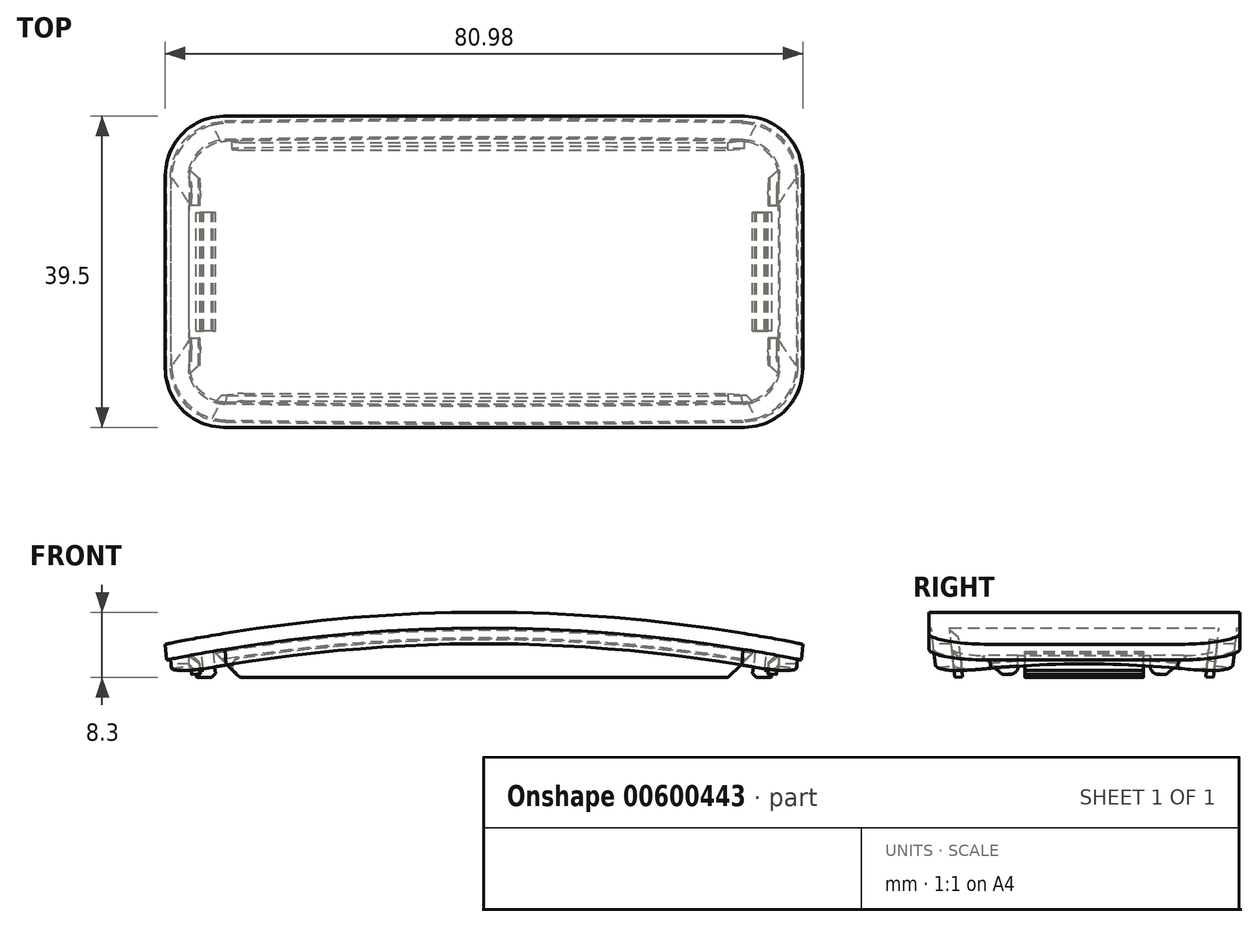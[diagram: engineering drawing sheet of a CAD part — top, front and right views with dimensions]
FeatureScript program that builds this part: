
annotation { "Feature Type Name" : "Feature", "Feature Type Description" : "" }
export const myFeature = defineFeature(function(context is Context, id is Id, definition is map)
    precondition{}
    {
        {
            var Q0;
            Q0=qCreatedBy(makeId("Top.planeOp"),FACE);
            var sketch = newSketch(context, id + "F0", { "sketchPlane" : qUnion([Q0])});
            skLineSegment(sketch, "E0.bottom", {"start": v(-32.64, 18.78) * mm, "end": v(32.64, 18.78) * mm});
            skLineSegment(sketch, "E0.top", {"start": v(-32.64, -18.78) * mm, "end": v(32.64, -18.78) * mm});
            skLineSegment(sketch, "E0.left", {"start": v(-39.64, 11.78) * mm, "end": v(-39.64, -11.78) * mm});
            skLineSegment(sketch, "E0.right", {"start": v(39.64, 11.78) * mm, "end": v(39.64, -11.78) * mm});
            skPoint(sketch, "E0.middle", {"position": v(0, 0) * mm});
            skPoint(sketch, "E1.visualSharp", {"position": v(-39.64, 18.78) * mm});
            skArc(sketch, "E1.filletArc", {"start": v(-32.64, 18.78) * mm, "mid": v(-37.59, 16.73) * mm, "end": v(-39.64, 11.78) * mm});
            skPoint(sketch, "E2.visualSharp", {"position": v(39.64, 18.78) * mm});
            skArc(sketch, "E2.filletArc", {"start": v(39.64, 11.78) * mm, "mid": v(37.59, 16.73) * mm, "end": v(32.64, 18.78) * mm});
            skPoint(sketch, "E3.visualSharp", {"position": v(39.64, -18.78) * mm});
            skArc(sketch, "E3.filletArc", {"start": v(32.64, -18.78) * mm, "mid": v(37.59, -16.73) * mm, "end": v(39.64, -11.78) * mm});
            skPoint(sketch, "E4.visualSharp", {"position": v(-39.64, -18.78) * mm});
            skArc(sketch, "E4.filletArc", {"start": v(-39.64, -11.78) * mm, "mid": v(-37.59, -16.73) * mm, "end": v(-32.64, -18.78) * mm});
            skSolve(sketch);
        }
        {
            var Q0;
            Q0=qCreatedBy(makeId("Top.planeOp"),FACE);
            cPlane(context, id + "F1", {"entities" : qUnion([Q0]), "cplaneType" : CPlaneType.OFFSET, "offset" : 100 * mm, "width" : 150 * mm, "height" : 150 * mm});
        }
        {
            var Q0;
            Q0=qCreatedBy(id+"F1.planeOp",FACE);
            var sketch = newSketch(context, id + "F2", { "sketchPlane" : qUnion([Q0])});
            skLineSegment(sketch, "E5.bottom", {"start": v(-40.98, 29.29) * mm, "end": v(40.98, 29.29) * mm});
            skLineSegment(sketch, "E5.top", {"start": v(-40.98, -29.29) * mm, "end": v(40.98, -29.29) * mm});
            skLineSegment(sketch, "E5.left", {"start": v(-48.38, 21.9) * mm, "end": v(-48.38, -21.9) * mm});
            skLineSegment(sketch, "E5.right", {"start": v(48.38, 21.9) * mm, "end": v(48.38, -21.9) * mm});
            skPoint(sketch, "E5.middle", {"position": v(0, 0) * mm});
            skPoint(sketch, "E6.visualSharp", {"position": v(-48.38, 29.29) * mm});
            skArc(sketch, "E6.filletArc", {"start": v(-40.98, 29.29) * mm, "mid": v(-46.22, 27.12) * mm, "end": v(-48.38, 21.9) * mm});
            skPoint(sketch, "E7.visualSharp", {"position": v(48.38, 29.29) * mm});
            skArc(sketch, "E7.filletArc", {"start": v(48.38, 21.9) * mm, "mid": v(46.22, 27.12) * mm, "end": v(40.98, 29.29) * mm});
            skPoint(sketch, "E8.visualSharp", {"position": v(48.38, -29.3) * mm});
            skArc(sketch, "E8.filletArc", {"start": v(40.98, -29.29) * mm, "mid": v(46.22, -27.12) * mm, "end": v(48.38, -21.9) * mm});
            skPoint(sketch, "E9.visualSharp", {"position": v(-48.38, -29.3) * mm});
            skArc(sketch, "E9.filletArc", {"start": v(-48.38, -21.9) * mm, "mid": v(-46.22, -27.12) * mm, "end": v(-40.98, -29.29) * mm});
            skSolve(sketch);
        }
        {
            var Q0;
            Q0=makeQuery(id+"F0.imprint","IMPRINT",FACE,{"disambiguationData":[TD([[makeQuery(id+"F0.imprint","IMPRINT",EDGE,{"derivedFrom":sQuery(id+"F0.wireOp",EDGE,"E0.bottom")}),-1.0]])]});
            var Q1;
            Q1=makeQuery(id+"F2.imprint","IMPRINT",FACE,{"disambiguationData":[TD([[makeQuery(id+"F2.imprint","IMPRINT",EDGE,{"derivedFrom":sQuery(id+"F2.wireOp",EDGE,"E5.bottom")}),-1.0]])]});
            loft(context, id + "F3", {"sheetProfilesArray" : [{ "sheetProfileEntities" : qUnion([Q0]) }, { "sheetProfileEntities" : qUnion([Q1]) }]});
        }
        {
            var Q0;
            Q0=makeQuery(id+"F3.opLoft","CAP_FACE",FACE,{"disambiguationData":[OSD([makeQuery(id+"F0.imprint","IMPRINT",FACE,{"disambiguationData":[TD([[makeQuery(id+"F0.imprint","IMPRINT",EDGE,{"derivedFrom":sQuery(id+"F0.wireOp",EDGE,"E0.bottom")}),-1.0]])]})])],"isStart":true});
            var Q1;
            Q1=makeQuery(id+"F3.opLoft","CAP_FACE",FACE,{"disambiguationData":[OSD([makeQuery(id+"F2.imprint","IMPRINT",FACE,{"disambiguationData":[TD([[makeQuery(id+"F2.imprint","IMPRINT",EDGE,{"derivedFrom":sQuery(id+"F2.wireOp",EDGE,"E5.bottom")}),-1.0]])]})])],"isStart":true});
            shell(context, id + "F4", {"entities" : qUnion([Q0, Q1]), "thickness" : 2.3 * mm});
        }
        {
            var Q0;
            Q0=qCreatedBy(makeId("Front.planeOp"),FACE);
            var sketch = newSketch(context, id + "F5", { "sketchPlane" : qUnion([Q0])});
            skArc(sketch, "E10", {"start": v(39.64, 0) * mm, "mid": v(0, 3.97) * mm, "end": v(-39.64, 0) * mm});
            skLineSegment(sketch, "E11", {"start": v(-39.64, 0) * mm, "end": v(39.64, 0) * mm});
            skSolve(sketch);
        }
        {
            var Q0;
            Q0=qSketchRegion(id+"F5",true);
            var Q1;
            Q1=makeQuery(id+"F3.opLoft","SWEPT_FACE",FACE,{"disambiguationData":[OSD([sQuery(id+"F0.wireOp",EDGE,"E0.bottom"),sQuery(id+"F0.wireOp",EDGE,"E1.filletArc"),sQuery(id+"F0.wireOp",EDGE,"E2.filletArc"),sQuery(id+"F2.wireOp",EDGE,"E5.bottom"),sQuery(id+"F2.wireOp",EDGE,"E6.filletArc"),sQuery(id+"F2.wireOp",EDGE,"E7.filletArc")])]});
            var Q2;
            Q2=makeQuery(id+"F3.opLoft","SWEPT_FACE",FACE,{"disambiguationData":[OSD([sQuery(id+"F0.wireOp",EDGE,"E0.top"),sQuery(id+"F0.wireOp",EDGE,"E3.filletArc"),sQuery(id+"F0.wireOp",EDGE,"E4.filletArc"),sQuery(id+"F2.wireOp",EDGE,"E5.top"),sQuery(id+"F2.wireOp",EDGE,"E8.filletArc"),sQuery(id+"F2.wireOp",EDGE,"E9.filletArc")])]});
            extrude(context, id + "F6", {"entities" : qUnion([Q0]), "operationType" : NewBodyOperationType.REMOVE, "endBound" : BoundingType.UP_TO_SURFACE, "oppositeDirection" : true, "depth" : 25 * mm, "endBoundEntityFace" : qUnion([Q1]), "offsetDistance" : 25 * mm, "hasSecondDirection" : true, "secondDirectionBound" : SecondDirectionBoundingType.UP_TO_SURFACE, "secondDirectionOppositeDirection" : false, "secondDirectionDepth" : 25 * mm, "secondDirectionBoundEntityFace" : qUnion([Q2])});
        }
        {
            var Q0;
            Q0=qCreatedBy(makeId("Right.planeOp"),FACE);
            var sketch = newSketch(context, id + "F7", { "sketchPlane" : qUnion([Q0])});
            skArc(sketch, "E12", {"start": v(18.78, 0) * mm, "mid": v(0, 1.42) * mm, "end": v(-18.78, 0) * mm});
            skLineSegment(sketch, "E13", {"start": v(-18.78, 0) * mm, "end": v(18.78, 0) * mm});
            skSolve(sketch);
        }
        {
            var Q0;
            Q0=qSketchRegion(id+"F7",true);
            var Q1;
            Q1=makeQuery(id+"F3.opLoft","SWEPT_FACE",FACE,{"disambiguationData":[OSD([sQuery(id+"F0.wireOp",EDGE,"E0.right"),sQuery(id+"F0.wireOp",EDGE,"E2.filletArc"),sQuery(id+"F0.wireOp",EDGE,"E3.filletArc"),sQuery(id+"F2.wireOp",EDGE,"E5.right"),sQuery(id+"F2.wireOp",EDGE,"E7.filletArc"),sQuery(id+"F2.wireOp",EDGE,"E8.filletArc")])]});
            var Q2;
            Q2=makeQuery(id+"F3.opLoft","SWEPT_FACE",FACE,{"disambiguationData":[OSD([sQuery(id+"F0.wireOp",EDGE,"E0.left"),sQuery(id+"F0.wireOp",EDGE,"E1.filletArc"),sQuery(id+"F0.wireOp",EDGE,"E4.filletArc"),sQuery(id+"F2.wireOp",EDGE,"E5.left"),sQuery(id+"F2.wireOp",EDGE,"E6.filletArc"),sQuery(id+"F2.wireOp",EDGE,"E9.filletArc")])]});
            extrude(context, id + "F8", {"entities" : qUnion([Q0]), "operationType" : NewBodyOperationType.REMOVE, "endBound" : BoundingType.UP_TO_SURFACE, "depth" : 25 * mm, "endBoundEntityFace" : qUnion([Q1]), "offsetDistance" : 25 * mm, "hasSecondDirection" : true, "secondDirectionBound" : SecondDirectionBoundingType.UP_TO_SURFACE, "secondDirectionOppositeDirection" : true, "secondDirectionDepth" : 25 * mm, "secondDirectionBoundEntityFace" : qUnion([Q2])});
        }
        {
            var Q0;
            Q0=makeQuery(id+"F8.boolean.opBoolean","INTERSECT",EDGE,{"disambiguationData":[OD(2.0)],"derivedFrom":[makeQuery(id+"F6.boolean.opBoolean","COPY",FACE,{"derivedFrom":makeQuery(id+"F6.opExtrude","SWEPT_FACE",FACE,{"disambiguationData":[OSD([sQuery(id+"F5.wireOp",EDGE,"E10")])]})}),makeQuery(id+"F8.opExtrude","SWEPT_FACE",FACE,{"disambiguationData":[OSD([sQuery(id+"F7.wireOp",EDGE,"E12")])]})]});
            var Q1;
            Q1=makeQuery(id+"F8.boolean.opBoolean","INTERSECT",EDGE,{"disambiguationData":[OD(3.0)],"derivedFrom":[makeQuery(id+"F6.boolean.opBoolean","COPY",FACE,{"derivedFrom":makeQuery(id+"F6.opExtrude","SWEPT_FACE",FACE,{"disambiguationData":[OSD([sQuery(id+"F5.wireOp",EDGE,"E10")])]})}),makeQuery(id+"F8.opExtrude","SWEPT_FACE",FACE,{"disambiguationData":[OSD([sQuery(id+"F7.wireOp",EDGE,"E12")])]})]});
            var Q2;
            Q2=makeQuery(id+"F8.boolean.opBoolean","INTERSECT",EDGE,{"disambiguationData":[OD(0.0)],"derivedFrom":[makeQuery(id+"F6.boolean.opBoolean","COPY",FACE,{"derivedFrom":makeQuery(id+"F6.opExtrude","SWEPT_FACE",FACE,{"disambiguationData":[OSD([sQuery(id+"F5.wireOp",EDGE,"E10")])]})}),makeQuery(id+"F8.opExtrude","SWEPT_FACE",FACE,{"disambiguationData":[OSD([sQuery(id+"F7.wireOp",EDGE,"E12")])]})]});
            var Q3;
            Q3=makeQuery(id+"F8.boolean.opBoolean","INTERSECT",EDGE,{"disambiguationData":[OD(1.0)],"derivedFrom":[makeQuery(id+"F6.boolean.opBoolean","COPY",FACE,{"derivedFrom":makeQuery(id+"F6.opExtrude","SWEPT_FACE",FACE,{"disambiguationData":[OSD([sQuery(id+"F5.wireOp",EDGE,"E10")])]})}),makeQuery(id+"F8.opExtrude","SWEPT_FACE",FACE,{"disambiguationData":[OSD([sQuery(id+"F7.wireOp",EDGE,"E12")])]})]});
            fillet(context, id + "F9", {"entities" : qUnion([Q0, Q1, Q2, Q3]), "radius" : 40 * mm, "tangentPropagation" : true, "allowEdgeOverflow" : false});
        }
        {
            var Q0;
            Q0=qCreatedBy(makeId("Front.planeOp"),FACE);
            var sketch = newSketch(context, id + "F10", { "sketchPlane" : qUnion([Q0])});
            skLineSegment(sketch, "E14.bottom", {"start": v(-48.38, 100) * mm, "end": v(48.38, 100) * mm});
            skLineSegment(sketch, "E14.top", {"start": v(-48.38, 20.57) * mm, "end": v(48.38, 20.57) * mm});
            skLineSegment(sketch, "E14.left", {"start": v(-48.38, 100) * mm, "end": v(-48.38, 20.57) * mm});
            skLineSegment(sketch, "E14.right", {"start": v(48.38, 100) * mm, "end": v(48.38, 20.57) * mm});
            skSolve(sketch);
        }
        {
            var Q0;
            Q0=qSketchRegion(id+"F10",true);
            var Q1;
            Q1=makeQuery(id+"F3.opLoft","SWEPT_FACE",FACE,{"disambiguationData":[OSD([sQuery(id+"F0.wireOp",EDGE,"E0.bottom"),sQuery(id+"F0.wireOp",EDGE,"E1.filletArc"),sQuery(id+"F0.wireOp",EDGE,"E2.filletArc"),sQuery(id+"F2.wireOp",EDGE,"E5.bottom"),sQuery(id+"F2.wireOp",EDGE,"E6.filletArc"),sQuery(id+"F2.wireOp",EDGE,"E7.filletArc")])]});
            var Q2;
            Q2=makeQuery(id+"F3.opLoft","SWEPT_FACE",FACE,{"disambiguationData":[OSD([sQuery(id+"F0.wireOp",EDGE,"E0.top"),sQuery(id+"F0.wireOp",EDGE,"E3.filletArc"),sQuery(id+"F0.wireOp",EDGE,"E4.filletArc"),sQuery(id+"F2.wireOp",EDGE,"E5.top"),sQuery(id+"F2.wireOp",EDGE,"E8.filletArc"),sQuery(id+"F2.wireOp",EDGE,"E9.filletArc")])]});
            extrude(context, id + "F11", {"entities" : qUnion([Q0]), "operationType" : NewBodyOperationType.REMOVE, "endBound" : BoundingType.UP_TO_SURFACE, "oppositeDirection" : true, "depth" : 25 * mm, "endBoundEntityFace" : qUnion([Q1]), "offsetDistance" : 25 * mm, "hasSecondDirection" : true, "secondDirectionBound" : SecondDirectionBoundingType.UP_TO_SURFACE, "secondDirectionOppositeDirection" : false, "secondDirectionDepth" : 25 * mm, "secondDirectionBoundEntityFace" : qUnion([Q2])});
        }
        {
            var Q0;
            Q0=makeQuery(id+"F4.opShell","OFFSET_FACE",FACE,{"disambiguationData":[OSD([sQuery(id+"F0.wireOp",EDGE,"E0.bottom"),sQuery(id+"F0.wireOp",EDGE,"E1.filletArc"),sQuery(id+"F0.wireOp",EDGE,"E2.filletArc"),sQuery(id+"F2.wireOp",EDGE,"E5.bottom"),sQuery(id+"F2.wireOp",EDGE,"E6.filletArc"),sQuery(id+"F2.wireOp",EDGE,"E7.filletArc")])]});
            var sketch = newSketch(context, id + "F12", { "sketchPlane" : qUnion([Q0])});
            skArc(sketch, "E15", {"start": v(33.1, 3.47) * mm, "mid": v(0, 6.2) * mm, "end": v(-33.1, 3.47) * mm});
            skLineSegment(sketch, "E16", {"start": v(31.01, 1.4) * mm, "end": v(33.1, 3.47) * mm});
            skLineSegment(sketch, "E17", {"start": v(0, 6.2) * mm, "end": v(0, 5.7) * mm, "construction": true});
            skLineSegment(sketch, "E18", {"start": v(0, 5.7) * mm, "end": v(0, 1.4) * mm, "construction": true});
            skLineSegment(sketch, "E19", {"start": v(-33.1, 3.47) * mm, "end": v(-31.01, 1.4) * mm});
            skLineSegment(sketch, "E20", {"start": v(33.1, 3.47) * mm, "end": v(31.01, 1.4) * mm});
            skLineSegment(sketch, "E21", {"start": v(-31.01, 1.4) * mm, "end": v(31.01, 1.4) * mm});
            skSolve(sketch);
        }
        {
            var Q0;
            Q0=qSketchRegion(id+"F12",true);
            extrude(context, id + "F13", {"entities" : qUnion([Q0]), "depth" : 1 * mm, "offsetDistance" : 25 * mm});
        }
        {
            var Q0;
            Q0=makeQuery(id+"F13.opExtrude","SWEPT_BODY",BODY,{"disambiguationData":[OSD([sQuery(id+"F12.wireOp",EDGE,"E15"),sQuery(id+"F12.wireOp",EDGE,"fm1ZzIcU-osaq-4KBk-rcFe-HOcxulJE4Vdi"),sQuery(id+"F12.wireOp",EDGE,"E19"),sQuery(id+"F12.wireOp",EDGE,"E20")])]});
            var Q1;
            Q1=qCreatedBy(makeId("Front.planeOp"),FACE);
            mirror(context, id + "F14", {"operationType" : NewBodyOperationType.ADD, "entities" : qUnion([Q0]), "mirrorPlane" : qUnion([Q1])});
        }
        {
            var Q0;
            Q0=makeQuery(id+"F4.opShell","OFFSET_FACE",FACE,{"disambiguationData":[OSD([sQuery(id+"F0.wireOp",EDGE,"E0.left"),sQuery(id+"F0.wireOp",EDGE,"E1.filletArc"),sQuery(id+"F0.wireOp",EDGE,"E4.filletArc"),sQuery(id+"F2.wireOp",EDGE,"E5.left"),sQuery(id+"F2.wireOp",EDGE,"E6.filletArc"),sQuery(id+"F2.wireOp",EDGE,"E9.filletArc")])]});
            var sketch = newSketch(context, id + "F15", { "sketchPlane" : qUnion([Q0])});
            skArc(sketch, "E22", {"start": v(11.9, 4.62) * mm, "mid": v(0, 5.18) * mm, "end": v(-11.9, 4.62) * mm});
            skLineSegment(sketch, "E23", {"start": v(0, 4.68) * mm, "end": v(0, 5.18) * mm, "construction": true});
            skLineSegment(sketch, "E24", {"start": v(-11.9, 4.62) * mm, "end": v(-10.4, 3.25) * mm});
            skLineSegment(sketch, "E25", {"start": v(11.9, 4.62) * mm, "end": v(10.4, 3.25) * mm});
            skArc(sketch, "E26", {"start": v(10.4, 3.25) * mm, "mid": v(0, 3.68) * mm, "end": v(-10.4, 3.25) * mm});
            skLineSegment(sketch, "E27", {"start": v(8.4, 3.4) * mm, "end": v(8.4, 4.9) * mm});
            skLineSegment(sketch, "E28", {"start": v(-8.4, 3.4) * mm, "end": v(-8.4, 4.9) * mm});
            skSolve(sketch);
        }
        {
            var Q0;
            {var subQ7=sQuery(id+"F15.wireOp",EDGE,"E26");var subQ9=sQuery(id+"F15.wireOp",EDGE,"E25");var subQ10=makeQuery(id+"F15.imprint","INTERSECT",VERTEX,{"derivedFrom":[subQ9,subQ7]});Q0=makeQuery(id+"F15.imprint","IMPRINT",FACE,{"disambiguationData":[TD([[makeQuery(id+"F15.imprint","IMPRINT",EDGE,{"disambiguationData":[TD([[subQ10,-1.0]])],"derivedFrom":subQ7}),-1.0]])]});}
            var Q1;
            {var subQ0=sQuery(id+"F15.wireOp",EDGE,"E27");var subQ1=sQuery(id+"F15.wireOp",EDGE,"E22");var subQ2=makeQuery(id+"F15.imprint","INTERSECT",VERTEX,{"derivedFrom":[subQ1,subQ0]});Q1=makeQuery(id+"F15.imprint","IMPRINT",FACE,{"disambiguationData":[TD([[makeQuery(id+"F15.imprint","IMPRINT",EDGE,{"disambiguationData":[TD([[subQ2,1.0]])],"derivedFrom":subQ1}),1.0]])]});}
            var Q2;
            {var subQ7=sQuery(id+"F15.wireOp",EDGE,"E26");var subQ9=sQuery(id+"F15.wireOp",EDGE,"E24");var subQ10=makeQuery(id+"F15.imprint","INTERSECT",VERTEX,{"derivedFrom":[subQ9,subQ7]});Q2=makeQuery(id+"F15.imprint","IMPRINT",FACE,{"disambiguationData":[TD([[makeQuery(id+"F15.imprint","IMPRINT",EDGE,{"disambiguationData":[TD([[subQ10,1.0]])],"derivedFrom":subQ7}),-1.0]])]});}
            var Q3;
            {var subQ9=sQuery(id+"F15.wireOp",EDGE,"E28");var subQ11=sQuery(id+"F15.wireOp",EDGE,"E22");var subQ12=makeQuery(id+"F15.imprint","INTERSECT",VERTEX,{"derivedFrom":[subQ11,subQ9]});Q3=makeQuery(id+"F15.imprint","IMPRINT",FACE,{"disambiguationData":[TD([[makeQuery(id+"F15.imprint","IMPRINT",EDGE,{"disambiguationData":[TD([[subQ12,-1.0]])],"derivedFrom":subQ11}),1.0]])]});}
            extrude(context, id + "F16", {"entities" : qUnion([Q0, Q1, Q2, Q3]), "depth" : 1.3 * mm, "offsetDistance" : 25 * mm});
        }
        {
            var Q0;
            Q0=makeQuery(id+"F16.opExtrude","SWEPT_BODY",BODY,{"disambiguationData":[OSD([sQuery(id+"F15.wireOp",EDGE,"E22"),sQuery(id+"F15.wireOp",EDGE,"E24"),sQuery(id+"F15.wireOp",EDGE,"E25"),sQuery(id+"F15.wireOp",EDGE,"E26")])]});
            var Q1;
            Q1=qCreatedBy(makeId("Right.planeOp"),FACE);
            mirror(context, id + "F17", {"operationType" : NewBodyOperationType.ADD, "entities" : qUnion([Q0]), "mirrorPlane" : qUnion([Q1])});
        }
        {
            var Q0;
            Q0=makeQuery(id+"F16.opExtrude","CAP_FACE",FACE,{"disambiguationData":[OSD([sQuery(id+"F15.wireOp",EDGE,"E22"),sQuery(id+"F15.wireOp",EDGE,"E25"),sQuery(id+"F15.wireOp",EDGE,"E26"),sQuery(id+"F15.wireOp",EDGE,"E27")])],"isStart":true});
            var Q1;
            Q1=makeQuery(id+"F16.opExtrude","CAP_FACE",FACE,{"disambiguationData":[OSD([sQuery(id+"F15.wireOp",EDGE,"E22"),sQuery(id+"F15.wireOp",EDGE,"E24"),sQuery(id+"F15.wireOp",EDGE,"E26"),sQuery(id+"F15.wireOp",EDGE,"E28")])],"isStart":true});
            extrude(context, id + "F18", {"entities" : qUnion([Q0, Q1]), "operationType" : NewBodyOperationType.REMOVE, "oppositeDirection" : true, "depth" : .2 * mm, "offsetDistance" : 25 * mm});
        }
        {
            var Q0;
            Q0=makeQuery(id+"F17.opPattern","COPY",FACE,{"derivedFrom":makeQuery(id+"F16.opExtrude","CAP_FACE",FACE,{"disambiguationData":[OSD([sQuery(id+"F15.wireOp",EDGE,"E22"),sQuery(id+"F15.wireOp",EDGE,"E25"),sQuery(id+"F15.wireOp",EDGE,"E26"),sQuery(id+"F15.wireOp",EDGE,"E27")])],"isStart":true}),"instanceName":"1"});
            var Q1;
            Q1=makeQuery(id+"F17.opPattern","COPY",FACE,{"derivedFrom":makeQuery(id+"F16.opExtrude","CAP_FACE",FACE,{"disambiguationData":[OSD([sQuery(id+"F15.wireOp",EDGE,"E22"),sQuery(id+"F15.wireOp",EDGE,"E24"),sQuery(id+"F15.wireOp",EDGE,"E26"),sQuery(id+"F15.wireOp",EDGE,"E28")])],"isStart":true}),"instanceName":"1"});
            extrude(context, id + "F19", {"entities" : qUnion([Q0, Q1]), "operationType" : NewBodyOperationType.REMOVE, "oppositeDirection" : true, "depth" : .2 * mm, "offsetDistance" : 25 * mm});
        }
        {
            var Q0;
            Q0=makeQuery(id+"F16.opExtrude","CAP_EDGE",EDGE,{"disambiguationData":[OSD([sQuery(id+"F15.wireOp",EDGE,"E22")])],"isStart":true});
            var Q1;
            Q1=makeQuery(id+"F13.opExtrude","CAP_EDGE",EDGE,{"disambiguationData":[OSD([sQuery(id+"F12.wireOp",EDGE,"E15")])],"isStart":true});
            var Q2;
            Q2=makeQuery(id+"F17.opPattern","COPY",EDGE,{"derivedFrom":makeQuery(id+"F16.opExtrude","CAP_EDGE",EDGE,{"disambiguationData":[OSD([sQuery(id+"F15.wireOp",EDGE,"E22")])],"isStart":true}),"instanceName":"1"});
            var Q3;
            Q3=makeQuery(id+"F14.opPattern","COPY",EDGE,{"derivedFrom":makeQuery(id+"F13.opExtrude","CAP_EDGE",EDGE,{"disambiguationData":[OSD([sQuery(id+"F12.wireOp",EDGE,"E15")])],"isStart":true}),"instanceName":"1"});
            chamfer(context, id + "F20", {"entities" : qUnion([Q0, Q1, Q2, Q3]), "width" : 1.2 * mm, "tangentPropagation" : true});
        }
        {
            var Q0;
            Q0=makeQuery(id+"F13.opExtrude","SWEPT_EDGE",EDGE,{"disambiguationData":[OSD([sQuery(id+"F12.wireOp",EDGE,"fm1ZzIcU-osaq-4KBk-rcFe-HOcxulJE4Vdi"),sQuery(id+"F12.wireOp",EDGE,"E19")])]});
            var Q1;
            Q1=makeQuery(id+"F16.opExtrude","SWEPT_EDGE",EDGE,{"disambiguationData":[OSD([sQuery(id+"F15.wireOp",EDGE,"E25"),sQuery(id+"F15.wireOp",EDGE,"E26")])]});
            var Q2;
            Q2=makeQuery(id+"F13.opExtrude","SWEPT_EDGE",EDGE,{"disambiguationData":[OSD([sQuery(id+"F12.wireOp",EDGE,"fm1ZzIcU-osaq-4KBk-rcFe-HOcxulJE4Vdi"),sQuery(id+"F12.wireOp",EDGE,"E20")])]});
            var Q3;
            Q3=makeQuery(id+"F17.opPattern","COPY",EDGE,{"derivedFrom":makeQuery(id+"F16.opExtrude","SWEPT_EDGE",EDGE,{"disambiguationData":[OSD([sQuery(id+"F15.wireOp",EDGE,"E25"),sQuery(id+"F15.wireOp",EDGE,"E26")])]}),"instanceName":"1"});
            var Q4;
            Q4=makeQuery(id+"F17.opPattern","COPY",EDGE,{"derivedFrom":makeQuery(id+"F16.opExtrude","SWEPT_EDGE",EDGE,{"disambiguationData":[OSD([sQuery(id+"F15.wireOp",EDGE,"E24"),sQuery(id+"F15.wireOp",EDGE,"E26")])]}),"instanceName":"1"});
            var Q5;
            Q5=makeQuery(id+"F14.opPattern","COPY",EDGE,{"derivedFrom":makeQuery(id+"F13.opExtrude","SWEPT_EDGE",EDGE,{"disambiguationData":[OSD([sQuery(id+"F12.wireOp",EDGE,"fm1ZzIcU-osaq-4KBk-rcFe-HOcxulJE4Vdi"),sQuery(id+"F12.wireOp",EDGE,"E20")])]}),"instanceName":"1"});
            var Q6;
            Q6=makeQuery(id+"F14.opPattern","COPY",EDGE,{"derivedFrom":makeQuery(id+"F13.opExtrude","SWEPT_EDGE",EDGE,{"disambiguationData":[OSD([sQuery(id+"F12.wireOp",EDGE,"fm1ZzIcU-osaq-4KBk-rcFe-HOcxulJE4Vdi"),sQuery(id+"F12.wireOp",EDGE,"E19")])]}),"instanceName":"1"});
            var Q7;
            Q7=makeQuery(id+"F16.opExtrude","SWEPT_EDGE",EDGE,{"disambiguationData":[OSD([sQuery(id+"F15.wireOp",EDGE,"E24"),sQuery(id+"F15.wireOp",EDGE,"E26")])]});
            var Q8;
            Q8=makeQuery(id+"F16.opExtrude","SWEPT_EDGE",EDGE,{"disambiguationData":[OSD([sQuery(id+"F15.wireOp",EDGE,"E26"),sQuery(id+"F15.wireOp",EDGE,"E27")])]});
            var Q9;
            Q9=makeQuery(id+"F16.opExtrude","SWEPT_EDGE",EDGE,{"disambiguationData":[OSD([sQuery(id+"F15.wireOp",EDGE,"E26"),sQuery(id+"F15.wireOp",EDGE,"E28")])]});
            var Q10;
            Q10=makeQuery(id+"F17.opPattern","COPY",EDGE,{"derivedFrom":makeQuery(id+"F16.opExtrude","SWEPT_EDGE",EDGE,{"disambiguationData":[OSD([sQuery(id+"F15.wireOp",EDGE,"E26"),sQuery(id+"F15.wireOp",EDGE,"E28")])]}),"instanceName":"1"});
            var Q11;
            Q11=makeQuery(id+"F17.opPattern","COPY",EDGE,{"derivedFrom":makeQuery(id+"F16.opExtrude","SWEPT_EDGE",EDGE,{"disambiguationData":[OSD([sQuery(id+"F15.wireOp",EDGE,"E26"),sQuery(id+"F15.wireOp",EDGE,"E27")])]}),"instanceName":"1"});
            fillet(context, id + "F21", {"entities" : qUnion([Q0, Q1, Q2, Q3, Q4, Q5, Q6, Q7, Q8, Q9, Q10, Q11]), "radius" : 1 * mm, "tangentPropagation" : true, "allowEdgeOverflow" : false});
        }
        {
            var Q0;
            Q0=qCreatedBy(makeId("Front.planeOp"),FACE);
            var sketch = newSketch(context, id + "F22", { "sketchPlane" : qUnion([Q0])});
            skArc(sketch, "E29", {"start": v(41.94, 1.57) * mm, "mid": v(0, 5.97) * mm, "end": v(-41.94, 1.57) * mm});
            skLineSegment(sketch, "E30", {"start": v(-41.94, 1.57) * mm, "end": v(-41.94, 20.57) * mm});
            skLineSegment(sketch, "E31", {"start": v(-41.94, 20.57) * mm, "end": v(41.94, 20.57) * mm});
            skLineSegment(sketch, "E32", {"start": v(41.94, 20.57) * mm, "end": v(41.94, 1.57) * mm});
            skSolve(sketch);
        }
        {
            var Q0;
            Q0=qSketchRegion(id+"F22",true);
            var Q1;
            Q1=makeQuery(id+"F3.opLoft","SWEPT_FACE",FACE,{"disambiguationData":[OSD([sQuery(id+"F0.wireOp",EDGE,"E0.bottom"),sQuery(id+"F0.wireOp",EDGE,"E1.filletArc"),sQuery(id+"F0.wireOp",EDGE,"E2.filletArc"),sQuery(id+"F2.wireOp",EDGE,"E5.bottom"),sQuery(id+"F2.wireOp",EDGE,"E6.filletArc"),sQuery(id+"F2.wireOp",EDGE,"E7.filletArc")])]});
            var Q2;
            Q2=makeQuery(id+"F3.opLoft","SWEPT_FACE",FACE,{"disambiguationData":[OSD([sQuery(id+"F0.wireOp",EDGE,"E0.top"),sQuery(id+"F0.wireOp",EDGE,"E3.filletArc"),sQuery(id+"F0.wireOp",EDGE,"E4.filletArc"),sQuery(id+"F2.wireOp",EDGE,"E5.top"),sQuery(id+"F2.wireOp",EDGE,"E8.filletArc"),sQuery(id+"F2.wireOp",EDGE,"E9.filletArc")])]});
            extrude(context, id + "F23", {"entities" : qUnion([Q0]), "operationType" : NewBodyOperationType.REMOVE, "endBound" : BoundingType.UP_TO_SURFACE, "oppositeDirection" : true, "depth" : 25 * mm, "endBoundEntityFace" : qUnion([Q1]), "offsetDistance" : 25 * mm, "hasSecondDirection" : true, "secondDirectionBound" : SecondDirectionBoundingType.UP_TO_SURFACE, "secondDirectionOppositeDirection" : false, "secondDirectionDepth" : 25 * mm, "secondDirectionBoundEntityFace" : qUnion([Q2])});
        }
        {
            var Q0;
            Q0=qCreatedBy(makeId("Front.planeOp"),FACE);
            var sketch = newSketch(context, id + "F24", { "sketchPlane" : qUnion([Q0])});
            skArc(sketch, "E33", {"start": v(40.49, 3.9) * mm, "mid": v(0, 7.97) * mm, "end": v(-40.49, 3.9) * mm});
            skLineSegment(sketch, "E34", {"start": v(-40.31, 1.9) * mm, "end": v(-40.49, 3.9) * mm});
            skLineSegment(sketch, "E35", {"start": v(40.31, 1.9) * mm, "end": v(40.49, 3.9) * mm});
            skArc(sketch, "E36", {"start": v(40.31, 1.9) * mm, "mid": v(0, 5.97) * mm, "end": v(-40.31, 1.9) * mm});
            skLineSegment(sketch, "E37", {"start": v(0, 5.97) * mm, "end": v(0, 7.97) * mm, "construction": true});
            skLineSegment(sketch, "E38", {"start": v(39.71, 0.85) * mm, "end": v(39.81, 2) * mm, "construction": true});
            skSolve(sketch);
        }
        {
            var Q0;
            Q0=qSketchRegion(id+"F24",true);
            var Q1;
            Q1=makeQuery(id+"F3.opLoft","SWEPT_FACE",FACE,{"disambiguationData":[OSD([sQuery(id+"F0.wireOp",EDGE,"E0.top"),sQuery(id+"F0.wireOp",EDGE,"E3.filletArc"),sQuery(id+"F0.wireOp",EDGE,"E4.filletArc"),sQuery(id+"F2.wireOp",EDGE,"E5.top"),sQuery(id+"F2.wireOp",EDGE,"E8.filletArc"),sQuery(id+"F2.wireOp",EDGE,"E9.filletArc")])]});
            var Q2;
            Q2=makeQuery(id+"F3.opLoft","SWEPT_FACE",FACE,{"disambiguationData":[OSD([sQuery(id+"F0.wireOp",EDGE,"E0.bottom"),sQuery(id+"F0.wireOp",EDGE,"E1.filletArc"),sQuery(id+"F0.wireOp",EDGE,"E2.filletArc"),sQuery(id+"F2.wireOp",EDGE,"E5.bottom"),sQuery(id+"F2.wireOp",EDGE,"E6.filletArc"),sQuery(id+"F2.wireOp",EDGE,"E7.filletArc")])]});
            extrude(context, id + "F25", {"entities" : qUnion([Q0]), "operationType" : NewBodyOperationType.ADD, "endBound" : BoundingType.SYMMETRIC, "depth" : 39.5 * mm, "endBoundEntityFace" : qUnion([Q1]), "offsetDistance" : 25 * mm, "hasSecondDirection" : true, "secondDirectionBound" : SecondDirectionBoundingType.UP_TO_SURFACE, "secondDirectionOppositeDirection" : true, "secondDirectionDepth" : 25 * mm, "secondDirectionBoundEntityFace" : qUnion([Q2])});
        }
        {
            var Q0;
            Q0=makeQuery(id+"F25.opExtrude","CAP_EDGE",EDGE,{"disambiguationData":[OSD([sQuery(id+"F24.wireOp",EDGE,"E34")])],"isStart":false});
            var Q1;
            Q1=makeQuery(id+"F25.opExtrude","CAP_EDGE",EDGE,{"disambiguationData":[OSD([sQuery(id+"F24.wireOp",EDGE,"E34")])],"isStart":true});
            var Q2;
            Q2=makeQuery(id+"F25.opExtrude","CAP_EDGE",EDGE,{"disambiguationData":[OSD([sQuery(id+"F24.wireOp",EDGE,"E35")])],"isStart":true});
            var Q3;
            Q3=makeQuery(id+"F25.opExtrude","CAP_EDGE",EDGE,{"disambiguationData":[OSD([sQuery(id+"F24.wireOp",EDGE,"E35")])],"isStart":false});
            fillet(context, id + "F26", {"entities" : qUnion([Q0, Q1, Q2, Q3]), "radius" : 7.5 * mm, "tangentPropagation" : true, "allowEdgeOverflow" : false});
        }
        {
            var Q0;
            Q0=qCreatedBy(makeId("Front.planeOp"),FACE);
            var sketch = newSketch(context, id + "F27", { "sketchPlane" : qUnion([Q0])});
            skLineSegment(sketch, "E39", {"start": v(-34.46, 3.19) * mm, "end": v(-34.12, 0.22) * mm});
            skLineSegment(sketch, "E40", {"start": v(-34.12, 0.22) * mm, "end": v(-34.6, -0.33) * mm});
            skLineSegment(sketch, "E41", {"start": v(-34.6, -0.33) * mm, "end": v(-36.35, -0.33) * mm});
            skLineSegment(sketch, "E42", {"start": v(-36.55, -0.13) * mm, "end": v(-36.55, 0.06) * mm});
            skLineSegment(sketch, "E43", {"start": v(-36.55, 0.06) * mm, "end": v(-36.05, 0.56) * mm});
            skLineSegment(sketch, "E44", {"start": v(-36.05, 0.56) * mm, "end": v(-35.65, 0.56) * mm});
            skLineSegment(sketch, "E45", {"start": v(-35.65, 0.56) * mm, "end": v(-35.91, 2.89) * mm});
            skLineSegment(sketch, "E46", {"start": v(-35.91, 2.89) * mm, "end": v(-34.46, 3.19) * mm});
            skPoint(sketch, "E47.visualSharp", {"position": v(-36.55, -0.33) * mm});
            skArc(sketch, "E47.filletArc", {"start": v(-36.55, -0.13) * mm, "mid": v(-36.49, -0.27) * mm, "end": v(-36.35, -0.33) * mm});
            skSolve(sketch);
        }
        {
            var Q0;
            Q0 = qSketchRegion(id + "F27", true);
            extrude(context, id + "F28", {"entities" : qUnion([Q0]), "endBound" : BoundingType.SYMMETRIC, "depth" : 15 * mm, "offsetDistance" : 25 * mm});
        }
        {
            var Q0;
            Q0=makeQuery(id+"F28.opExtrude","SWEPT_BODY",BODY,{"disambiguationData":[OSD([sQuery(id+"F27.wireOp",EDGE,"24c7c477-7aee-4d6f-a651-882b6b27d0f6"),sQuery(id+"F27.wireOp",EDGE,"E39"),sQuery(id+"F27.wireOp",EDGE,"E40"),sQuery(id+"F27.wireOp",EDGE,"E41"),sQuery(id+"F27.wireOp",EDGE,"E42"),sQuery(id+"F27.wireOp",EDGE,"E43"),sQuery(id+"F27.wireOp",EDGE,"E44"),sQuery(id+"F27.wireOp",EDGE,"E45"),sQuery(id+"F27.wireOp",EDGE,"17e5ed19-a9b8-47a1-a4b1-a6526e51fc24"),sQuery(id+"F27.wireOp",EDGE,"2f8a5ce5-8a27-4351-9590-e704de436a2a")])]});
            var Q1;
            Q1=qCreatedBy(makeId("Right.planeOp"),FACE);
            mirror(context, id + "F29", {"operationType" : NewBodyOperationType.ADD, "entities" : qUnion([Q0]), "mirrorPlane" : qUnion([Q1])});
        }
    });
